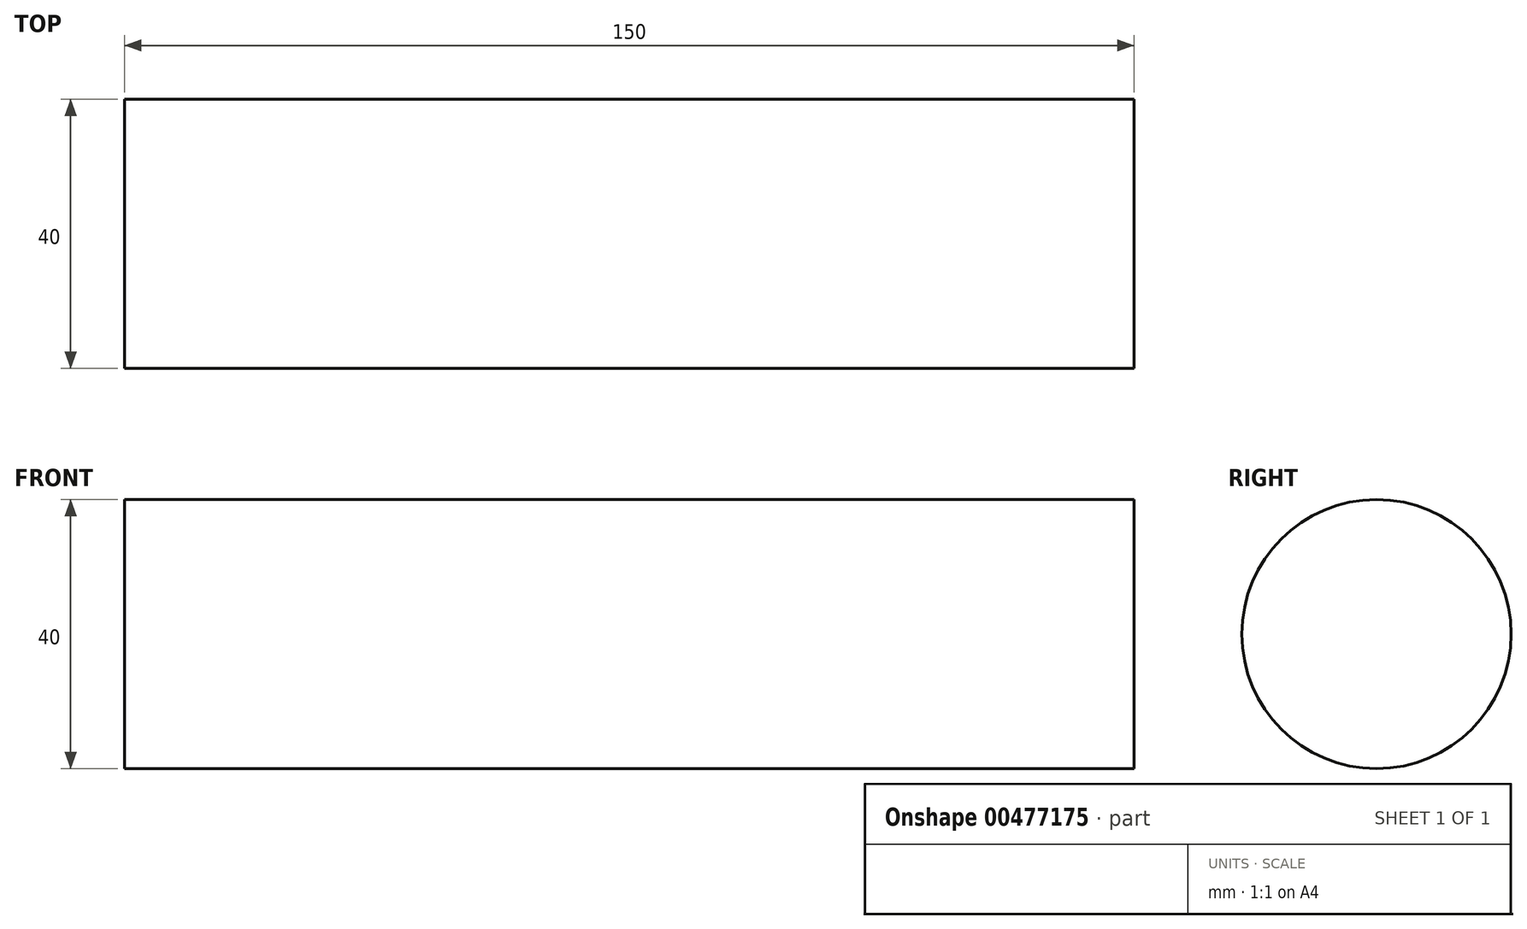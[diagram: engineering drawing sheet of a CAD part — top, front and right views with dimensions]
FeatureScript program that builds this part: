
annotation { "Feature Type Name" : "Feature", "Feature Type Description" : "" }
export const myFeature = defineFeature(function(context is Context, id is Id, definition is map)
    precondition{}
    {
        {
            var Q0;
            Q0=qCreatedBy(makeId("Right.planeOp"),FACE);
            var sketch = newSketch(context, id + "F0", { "sketchPlane" : qUnion([Q0])});
            skCircle(sketch, "E0", {"center": v(0, 0) * mm, "radius": 20 * mm});
            skSolve(sketch);
        }
        {
            var Q0;
            Q0=makeQuery(id+"F0.imprint","IMPRINT",FACE,{"disambiguationData":[TD([[makeQuery(id+"F0.imprint","IMPRINT",EDGE,{"derivedFrom":sQuery(id+"F0.wireOp",EDGE,"E0")}),1.0]])]});
            extrude(context, id + "F1", {"entities" : qUnion([Q0]), "depth" : 150 * mm});
        }
    });
